# Revit family: 2060688
name_source: partatom
category: Lighting Fixtures
revit_build: Autodesk Revit 2018 (Build: 20170223_1515(x64)
units: mm (PartAtom-declared; Revit-internal decimal feet)

## family parameters
Cut with Voids When Loaded = No
Host = Face
Light Source = Yes
OmniClass Number = 23.80.70.11.17
OmniClass Title = Specialized Lighting by Location or Use
Part Type = Normal
Room Calculation Point = No
Round Connector Dimension = Use Diameter
Shared = No

## types (1)
- 2060688 ASC100 II ARCH 630 4K IP65 DALI 120
    Aperture_SYL = 120 mm
    Apparent Load = 5 VA
    Assembly Code = D5020200
    AssetType = Fixed
    Color Filter = 16777215
    CutoutDiameter_SYL = 139 mm  [stored 0.456037 ft]
    Default Elevation = 0 mm  [stored 0 ft]
    Description = Direct LED retro fit for original LED 100 Deco (120) single CFL lamp offering Matching lumen levels and improved light distribution of original LED 100 CFL lamp equivalents Typically half the power consumption compared to CFL Up to 104lm/W 120mm aperture Decorative reflector accepts snap fit polycarbonate accessories from existing LED 100 Deco 120 offering New kometa accessory ring creates a diffused indirect halo of light onto the ceiling for decorative effect HE, HO and VHO versions equivalent of single 1 x 13W, 1 x 18W, 1 x 26W Additional VVHO versions which offer the performance circa 2 x 26W equivalent
    Diameter_SYL = 150 mm
    DiffuserRadius_SYL = 56 mm
    Dimming Lamp Color Temperature Shift = <None>
    DocumentationLiterature = http://www.sylvania-lighting.com
    DurationUnit = hours
    ElectricShockClassification = 126
    Emit Shape Visible in Rendering = No
    Emit from Circle Diameter = 112 mm
    ExpectedLife = 50000
    Height = 96 mm
    Height_SYL = 94 mm  [stored 0.308399 ft]
    IfcExportAs = Class II
    IfcExportType = IfcLightFixtureType
    ImpactProtectionIndex = IfcLightFixtureType
    IngressProtection = IfcLightFixtureType
    InputNominalFrequency = 4000
    InputVoltage = 0
    LampColourRenderingIndex = 16500
    LampColourTemperature = LED
    LampMacAdamStep = 80
    LampNominalLuminous = 4000 K
    LightOutputRatio = LED
    LuminaireType = 0
    ManufacturerName = 126 lm/W
    Material = Feilo Sylvania
    Material_1_SYL = Aluminum_Sylvania_Ascent_White
    Material_2_SYL = Polycarbonate_Sylvania_Ascent_Clear
    Material_3_SYL = Aluminium_Sylvania_Ascent_Silver
    Model = ASCENT 100 II ARCH 630 4K IP65 DALI 120
    ModelNumber = 2060688
    ModelReference = ASCENT 100 II ARCH 630 4K IP65 DALI 120
    Name = ASCENT 100 II ARCH 630 4K IP65 DALI 120
    NominalHeight = 94 mm  [stored 0.308399 ft]
    NominalLength = 169 mm  [stored 0.554462 ft]
    NominalWidth = 0 mm  [stored 0 ft]
    Outside Diameter = 168.9 mm
    Photometric Web File = 2060688.ies
    PowerConsumption = Lighting
    PowerFactor = 0
    Radius_SYL = 75 mm
    ReflectorRadius_SYL = 60 mm  [stored 0.19685 ft]
    Tilt Angle = -90°
    TypeName = ASCENT 100 II ARCH 630 4K IP65 DALI 120
    URL = 0.95
    Voltage = 0 V
    WarrantyDescription = http://www.sylvania-lighting.com

note: [stored X ft] marks values corroborated as IEEE doubles in the binary element streams (Revit-internal decimal feet)

## geometry (parser evidence)
native form markers: Blend x4, Sweep x2
no freeform markers — native parametric forms only
